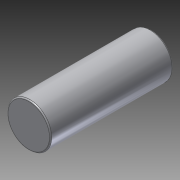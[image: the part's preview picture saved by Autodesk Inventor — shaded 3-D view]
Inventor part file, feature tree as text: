
AUTODESK INVENTOR PART (.ipt)
format: ipt  version: 2014 SP1 (Build 180222100, 222)  size: 94,720 bytes
history: native  units: in
note: dims shown in document units (in); Inventor stores cm internally (conversion verified against a paired STEP export)
features: extrude x2, sketch x1, thread x1, fillet x1
ambient origin geometry x8: Origin, YZ Plane, XZ Plane, XY Plane, X Axis, Y Axis, Z Axis, Center Point
bodies: Solid1 (feature_tree)
feature tree (5):
  sketch  "Sketch1"  dims[d0=2.5in d1=7.0in d2=0.0in d3=0.25in d4=1.0in d5=0.0in d6=1.0in d7=0.0in d8=0.0625in]
  extrude  "Extrusion1"  Depth=7.0in TaperAngle=0.0deg
  extrude  "Extrusion2"  Depth=0.0625in
  thread  "Thread1"  [1 undecoded]
  fillet  "Fillet1"  Radius=1.0in
note: 1 required parameter value undecoded (feature->parameter linkage not recoverable at this tier; creation-order binding heuristic only, values carry confidence <= 0.55)
